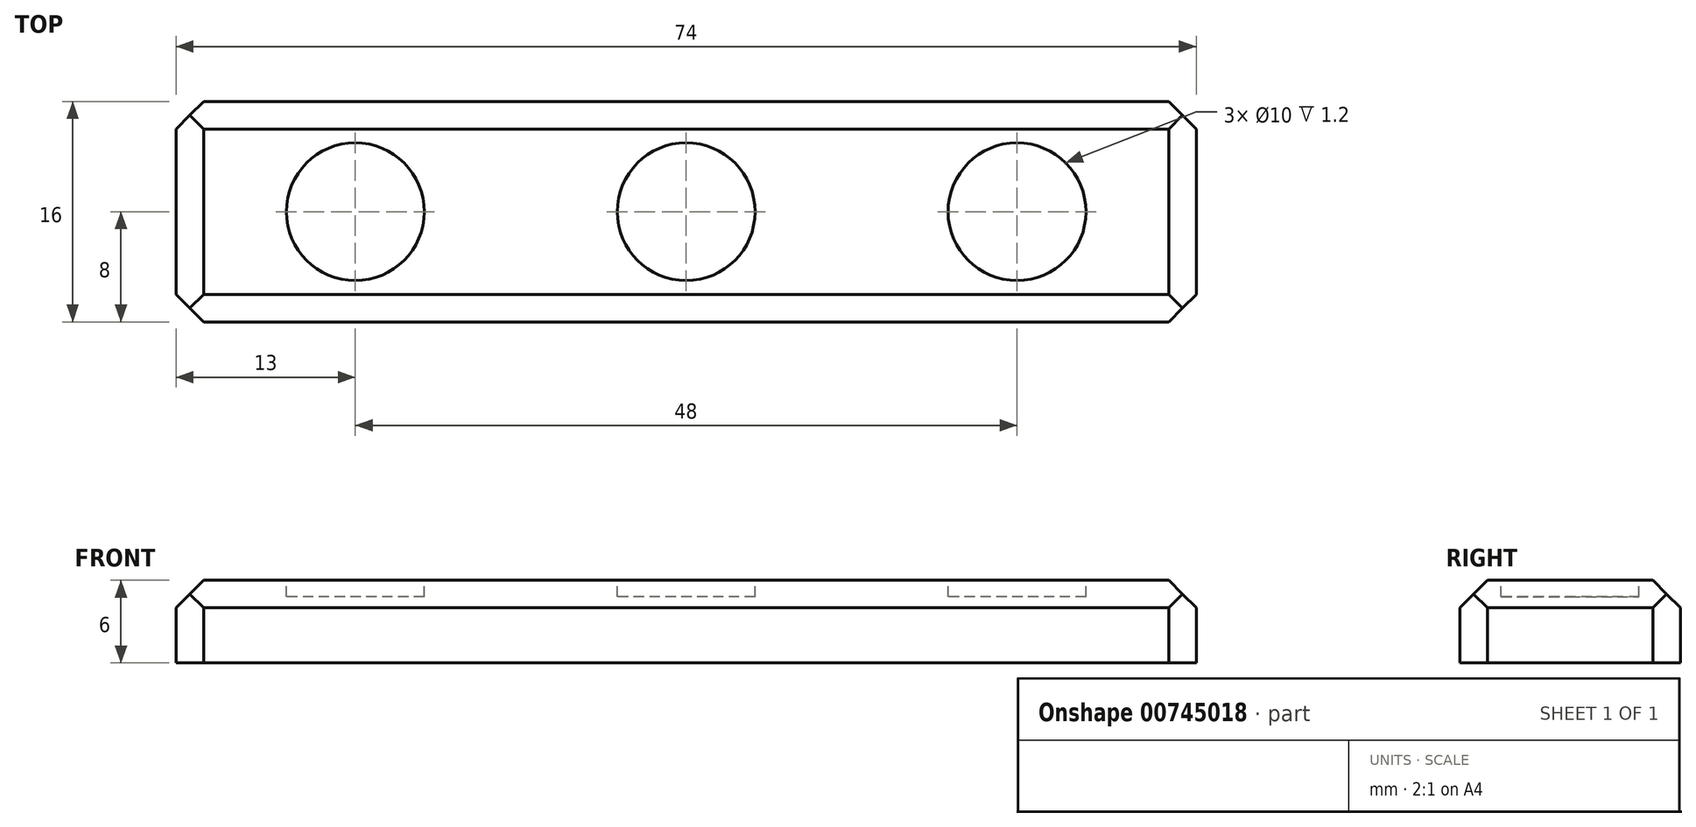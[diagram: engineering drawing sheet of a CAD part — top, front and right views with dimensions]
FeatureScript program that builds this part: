
annotation { "Feature Type Name" : "Feature", "Feature Type Description" : "" }
export const myFeature = defineFeature(function(context is Context, id is Id, definition is map)
    precondition{}
    {
        {
            var Q0;
            Q0=qCreatedBy(makeId("Top.planeOp"),FACE);
            var sketch = newSketch(context, id + "F0", { "sketchPlane" : qUnion([Q0])});
            skLineSegment(sketch, "E0.bottom", {"start": v(37, -8) * mm, "end": v(-37, -8) * mm});
            skLineSegment(sketch, "E0.top", {"start": v(37, 8) * mm, "end": v(-37, 8) * mm});
            skLineSegment(sketch, "E0.left", {"start": v(37, -8) * mm, "end": v(37, 8) * mm});
            skLineSegment(sketch, "E0.right", {"start": v(-37, -8) * mm, "end": v(-37, 8) * mm});
            skPoint(sketch, "E0.middle", {"position": v(0, 0) * mm});
            skSolve(sketch);
        }
        {
            var Q0;
            Q0=makeQuery(id+"F0.imprint","IMPRINT",FACE,{"disambiguationData":[TD([[makeQuery(id+"F0.imprint","IMPRINT",EDGE,{"derivedFrom":sQuery(id+"F0.wireOp",EDGE,"E0.bottom")}),-1.0]])]});
            extrude(context, id + "F1", {"entities" : qUnion([Q0]), "depth" : 6 * mm, "offsetDistance" : 25 * mm});
        }
        {
            var Q0;
            Q0=makeQuery(id+"F1.opExtrude","CAP_FACE",FACE,{"disambiguationData":[OSD([sQuery(id+"F0.wireOp",EDGE,"E0.bottom"),sQuery(id+"F0.wireOp",EDGE,"E0.top"),sQuery(id+"F0.wireOp",EDGE,"E0.left"),sQuery(id+"F0.wireOp",EDGE,"E0.right")])],"isStart":false});
            var sketch = newSketch(context, id + "F2", { "sketchPlane" : qUnion([Q0])});
            skCircle(sketch, "E1", {"center": v(-24, 0) * mm, "radius": 5 * mm});
            skCircle(sketch, "E2", {"center": v(24, 0) * mm, "radius": 5 * mm});
            skCircle(sketch, "E3", {"center": v(0, 0) * mm, "radius": 5 * mm});
            skSolve(sketch);
        }
        {
            var Q0;
            Q0=makeQuery(id+"F2.imprint","IMPRINT",FACE,{"disambiguationData":[TD([[makeQuery(id+"F2.imprint","IMPRINT",EDGE,{"derivedFrom":sQuery(id+"F2.wireOp",EDGE,"E1")}),1.0]])]});
            var Q1;
            Q1=makeQuery(id+"F2.imprint","IMPRINT",FACE,{"disambiguationData":[TD([[makeQuery(id+"F2.imprint","IMPRINT",EDGE,{"derivedFrom":sQuery(id+"F2.wireOp",EDGE,"E3")}),1.0]])]});
            var Q2;
            Q2=makeQuery(id+"F2.imprint","IMPRINT",FACE,{"disambiguationData":[TD([[makeQuery(id+"F2.imprint","IMPRINT",EDGE,{"derivedFrom":sQuery(id+"F2.wireOp",EDGE,"E2")}),1.0]])]});
            extrude(context, id + "F3", {"entities" : qUnion([Q0, Q1, Q2]), "operationType" : NewBodyOperationType.REMOVE, "oppositeDirection" : true, "depth" : 1.2 * mm, "offsetDistance" : 25 * mm});
        }
        {
            var Q0;
            Q0=makeQuery(id+"F1.opExtrude","SWEPT_EDGE",EDGE,{"disambiguationData":[OSD([sQuery(id+"F0.wireOp",EDGE,"E0.top"),sQuery(id+"F0.wireOp",EDGE,"E0.right")])]});
            var Q1;
            Q1=makeQuery(id+"F1.opExtrude","SWEPT_EDGE",EDGE,{"disambiguationData":[OSD([sQuery(id+"F0.wireOp",EDGE,"E0.bottom"),sQuery(id+"F0.wireOp",EDGE,"E0.right")])]});
            var Q2;
            Q2=makeQuery(id+"F1.opExtrude","SWEPT_EDGE",EDGE,{"disambiguationData":[OSD([sQuery(id+"F0.wireOp",EDGE,"E0.bottom"),sQuery(id+"F0.wireOp",EDGE,"E0.left")])]});
            var Q3;
            Q3=makeQuery(id+"F1.opExtrude","SWEPT_EDGE",EDGE,{"disambiguationData":[OSD([sQuery(id+"F0.wireOp",EDGE,"E0.top"),sQuery(id+"F0.wireOp",EDGE,"E0.left")])]});
            var Q4;
            Q4=makeQuery(id+"F1.opExtrude","CAP_EDGE",EDGE,{"disambiguationData":[OSD([sQuery(id+"F0.wireOp",EDGE,"E0.right")])],"isStart":false});
            var Q5;
            Q5=makeQuery(id+"F1.opExtrude","CAP_EDGE",EDGE,{"disambiguationData":[OSD([sQuery(id+"F0.wireOp",EDGE,"E0.left")])],"isStart":false});
            chamfer(context, id + "F4", {"entities" : qUnion([Q0, Q1, Q2, Q3, Q4, Q5]), "width" : 2 * mm, "tangentPropagation" : true});
        }
        {
            var Q0;
            Q0=makeQuery(id+"F1.opExtrude","CAP_EDGE",EDGE,{"disambiguationData":[OSD([sQuery(id+"F0.wireOp",EDGE,"E0.top")])],"isStart":false});
            var Q1;
            Q1=makeQuery(id+"F1.opExtrude","CAP_EDGE",EDGE,{"disambiguationData":[OSD([sQuery(id+"F0.wireOp",EDGE,"E0.bottom")])],"isStart":false});
            chamfer(context, id + "F5", {"entities" : qUnion([Q0, Q1]), "width" : 2 * mm, "tangentPropagation" : true});
        }
    });
